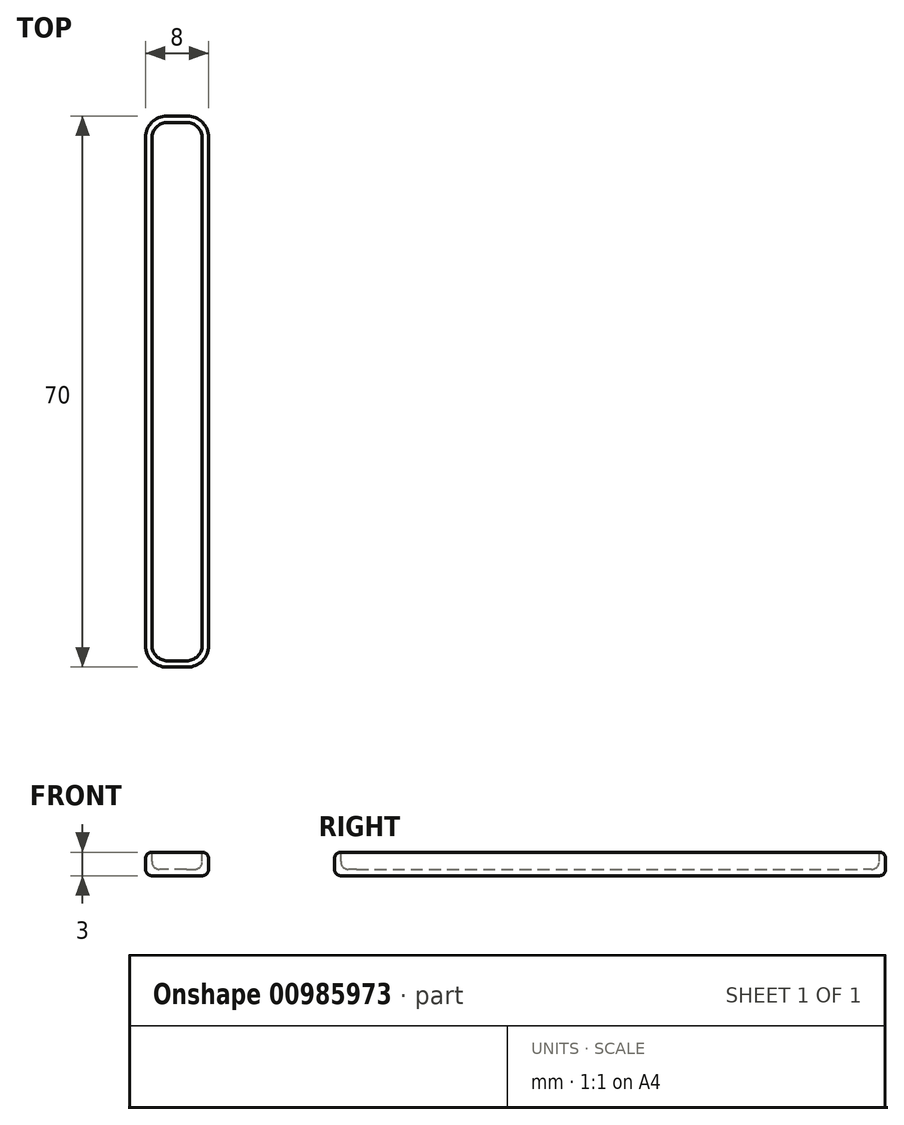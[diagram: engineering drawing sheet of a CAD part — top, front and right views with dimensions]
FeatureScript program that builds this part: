
annotation { "Feature Type Name" : "Feature", "Feature Type Description" : "" }
export const myFeature = defineFeature(function(context is Context, id is Id, definition is map)
    precondition{}
    {
        {
            var Q0;
            Q0=qCreatedBy(makeId("Top.planeOp"),FACE);
            var sketch = newSketch(context, id + "F0", { "sketchPlane" : qUnion([Q0])});
            skLineSegment(sketch, "E0.bottom", {"start": v(4, -35) * mm, "end": v(-4, -35) * mm});
            skLineSegment(sketch, "E0.top", {"start": v(4, 35) * mm, "end": v(-4, 35) * mm});
            skLineSegment(sketch, "E0.left", {"start": v(4, -35) * mm, "end": v(4, 35) * mm});
            skLineSegment(sketch, "E0.right", {"start": v(-4, -35) * mm, "end": v(-4, 35) * mm});
            skPoint(sketch, "E0.middle", {"position": v(0, 0) * mm});
            skSolve(sketch);
        }
        {
            var Q0;
            Q0=makeQuery(id+"F0.imprint","IMPRINT",FACE,{"disambiguationData":[TD([[makeQuery(id+"F0.imprint","IMPRINT",EDGE,{"derivedFrom":sQuery(id+"F0.wireOp",EDGE,"E0.bottom")}),-1.0]])]});
            extrude(context, id + "F1", {"entities" : qUnion([Q0]), "depth" : 3 * mm, "offsetDistance" : 25 * mm});
        }
        {
            var Q0;
            Q0=makeQuery(id+"F1.opExtrude","CAP_FACE",FACE,{"disambiguationData":[OSD([sQuery(id+"F0.wireOp",EDGE,"E0.bottom"),sQuery(id+"F0.wireOp",EDGE,"E0.top"),sQuery(id+"F0.wireOp",EDGE,"E0.left"),sQuery(id+"F0.wireOp",EDGE,"E0.right")])],"isStart":false});
            var sketch = newSketch(context, id + "F2", { "sketchPlane" : qUnion([Q0])});
            skLineSegment(sketch, "E1.0", {"start": v(-3.2, -34.2) * mm, "end": v(-3.2, 34.2) * mm});
            skLineSegment(sketch, "E1.1", {"start": v(3.2, -34.2) * mm, "end": v(-3.2, -34.2) * mm});
            skLineSegment(sketch, "E1.2", {"start": v(3.2, -34.2) * mm, "end": v(3.2, 34.2) * mm});
            skLineSegment(sketch, "E1.3", {"start": v(3.2, 34.2) * mm, "end": v(-3.2, 34.2) * mm});
            skSolve(sketch);
        }
        {
            var Q0;
            Q0=makeQuery(id+"F2.imprint","IMPRINT",FACE,{"disambiguationData":[TD([[makeQuery(id+"F2.imprint","IMPRINT",EDGE,{"derivedFrom":sQuery(id+"F2.wireOp",EDGE,"E1.0")}),-1.0]])]});
            extrude(context, id + "F3", {"entities" : qUnion([Q0]), "operationType" : NewBodyOperationType.REMOVE, "oppositeDirection" : true, "depth" : 2.2 * mm, "offsetDistance" : 25 * mm});
        }
        {
            var Q0;
            Q0=makeQuery(id+"F1.opExtrude","SWEPT_EDGE",EDGE,{"disambiguationData":[OSD([sQuery(id+"F0.wireOp",EDGE,"E0.bottom"),sQuery(id+"F0.wireOp",EDGE,"E0.left")])]});
            var Q1;
            Q1=makeQuery(id+"F1.opExtrude","SWEPT_EDGE",EDGE,{"disambiguationData":[OSD([sQuery(id+"F0.wireOp",EDGE,"E0.bottom"),sQuery(id+"F0.wireOp",EDGE,"E0.right")])]});
            var Q2;
            Q2=makeQuery(id+"F1.opExtrude","SWEPT_EDGE",EDGE,{"disambiguationData":[OSD([sQuery(id+"F0.wireOp",EDGE,"E0.top"),sQuery(id+"F0.wireOp",EDGE,"E0.right")])]});
            var Q3;
            Q3=makeQuery(id+"F1.opExtrude","SWEPT_EDGE",EDGE,{"disambiguationData":[OSD([sQuery(id+"F0.wireOp",EDGE,"E0.top"),sQuery(id+"F0.wireOp",EDGE,"E0.left")])]});
            fillet(context, id + "F4", {"entities" : qUnion([Q0, Q1, Q2, Q3]), "radius" : 2.7 * mm, "tangentPropagation" : true, "allowEdgeOverflow" : false});
        }
        {
            var Q0;
            Q0=makeQuery(id+"F3.boolean.opBoolean","COPY",EDGE,{"derivedFrom":makeQuery(id+"F3.opExtrude","SWEPT_EDGE",EDGE,{"disambiguationData":[OSD([sQuery(id+"F2.wireOp",EDGE,"E1.0"),sQuery(id+"F2.wireOp",EDGE,"E1.3")])]})});
            var Q1;
            Q1=makeQuery(id+"F3.boolean.opBoolean","COPY",EDGE,{"derivedFrom":makeQuery(id+"F3.opExtrude","SWEPT_EDGE",EDGE,{"disambiguationData":[OSD([sQuery(id+"F2.wireOp",EDGE,"E1.2"),sQuery(id+"F2.wireOp",EDGE,"E1.3")])]})});
            var Q2;
            Q2=makeQuery(id+"F3.boolean.opBoolean","COPY",EDGE,{"derivedFrom":makeQuery(id+"F3.opExtrude","SWEPT_EDGE",EDGE,{"disambiguationData":[OSD([sQuery(id+"F2.wireOp",EDGE,"E1.0"),sQuery(id+"F2.wireOp",EDGE,"E1.1")])]})});
            var Q3;
            Q3=makeQuery(id+"F3.boolean.opBoolean","COPY",EDGE,{"derivedFrom":makeQuery(id+"F3.opExtrude","SWEPT_EDGE",EDGE,{"disambiguationData":[OSD([sQuery(id+"F2.wireOp",EDGE,"E1.1"),sQuery(id+"F2.wireOp",EDGE,"E1.2")])]})});
            fillet(context, id + "F5", {"entities" : qUnion([Q0, Q1, Q2, Q3]), "radius" : 2 * mm, "tangentPropagation" : true, "allowEdgeOverflow" : false});
        }
        {
            var Q0;
            {var subQ0=sQuery(id+"F0.wireOp",EDGE,"E0.right");var subQ1=sQuery(id+"F0.wireOp",EDGE,"E0.bottom");Q0=makeQuery(id+"F4.opFillet","BLEND_EDGE",EDGE,{"blendedFrom":[makeQuery(id+"F1.opExtrude","SWEPT_EDGE",EDGE,{"disambiguationData":[OSD([subQ1,subQ0])]}),makeQuery(id+"F1.opExtrude","CAP_FACE",FACE,{"disambiguationData":[OSD([subQ1,sQuery(id+"F0.wireOp",EDGE,"E0.top"),sQuery(id+"F0.wireOp",EDGE,"E0.left"),subQ0])],"isStart":true})],"blendedInto":[makeQuery(id+"F1.opExtrude","CAP_FACE",FACE,{"disambiguationData":[OSD([subQ1,sQuery(id+"F0.wireOp",EDGE,"E0.top"),sQuery(id+"F0.wireOp",EDGE,"E0.left"),subQ0])],"isStart":true})]});}
            var Q1;
            {var subQ0=sQuery(id+"F0.wireOp",EDGE,"E0.right");var subQ1=sQuery(id+"F0.wireOp",EDGE,"E0.bottom");Q1=makeQuery(id+"F4.opFillet","BLEND_EDGE",EDGE,{"blendedFrom":[makeQuery(id+"F1.opExtrude","SWEPT_EDGE",EDGE,{"disambiguationData":[OSD([subQ1,subQ0])]}),makeQuery(id+"F1.opExtrude","CAP_FACE",FACE,{"disambiguationData":[OSD([subQ1,sQuery(id+"F0.wireOp",EDGE,"E0.top"),sQuery(id+"F0.wireOp",EDGE,"E0.left"),subQ0])],"isStart":false})],"blendedInto":[makeQuery(id+"F1.opExtrude","CAP_FACE",FACE,{"disambiguationData":[OSD([subQ1,sQuery(id+"F0.wireOp",EDGE,"E0.top"),sQuery(id+"F0.wireOp",EDGE,"E0.left"),subQ0])],"isStart":false})]});}
            fillet(context, id + "F6", {"entities" : qUnion([Q0, Q1]), "radius" : .8 * mm, "tangentPropagation" : true, "allowEdgeOverflow" : false});
        }
        {
            var Q0;
            {var subQ0=sQuery(id+"F2.wireOp",EDGE,"E1.1");var subQ1=sQuery(id+"F2.wireOp",EDGE,"E1.0");Q0=makeQuery(id+"F5.opFillet","BLEND_EDGE",EDGE,{"blendedFrom":[makeQuery(id+"F3.boolean.opBoolean","COPY",EDGE,{"derivedFrom":makeQuery(id+"F3.opExtrude","SWEPT_EDGE",EDGE,{"disambiguationData":[OSD([subQ1,subQ0])]})}),makeQuery(id+"F3.boolean.opBoolean","COPY",FACE,{"derivedFrom":makeQuery(id+"F3.opExtrude","CAP_FACE",FACE,{"disambiguationData":[OSD([subQ1,subQ0,sQuery(id+"F2.wireOp",EDGE,"E1.2"),sQuery(id+"F2.wireOp",EDGE,"E1.3")])],"isStart":false})})],"blendedInto":[makeQuery(id+"F3.boolean.opBoolean","COPY",FACE,{"derivedFrom":makeQuery(id+"F3.opExtrude","CAP_FACE",FACE,{"disambiguationData":[OSD([subQ1,subQ0,sQuery(id+"F2.wireOp",EDGE,"E1.2"),sQuery(id+"F2.wireOp",EDGE,"E1.3")])],"isStart":false})})]});}
            fillet(context, id + "F7", {"entities" : qUnion([Q0]), "radius" : 1 * mm, "tangentPropagation" : true, "allowEdgeOverflow" : false});
        }
    });
